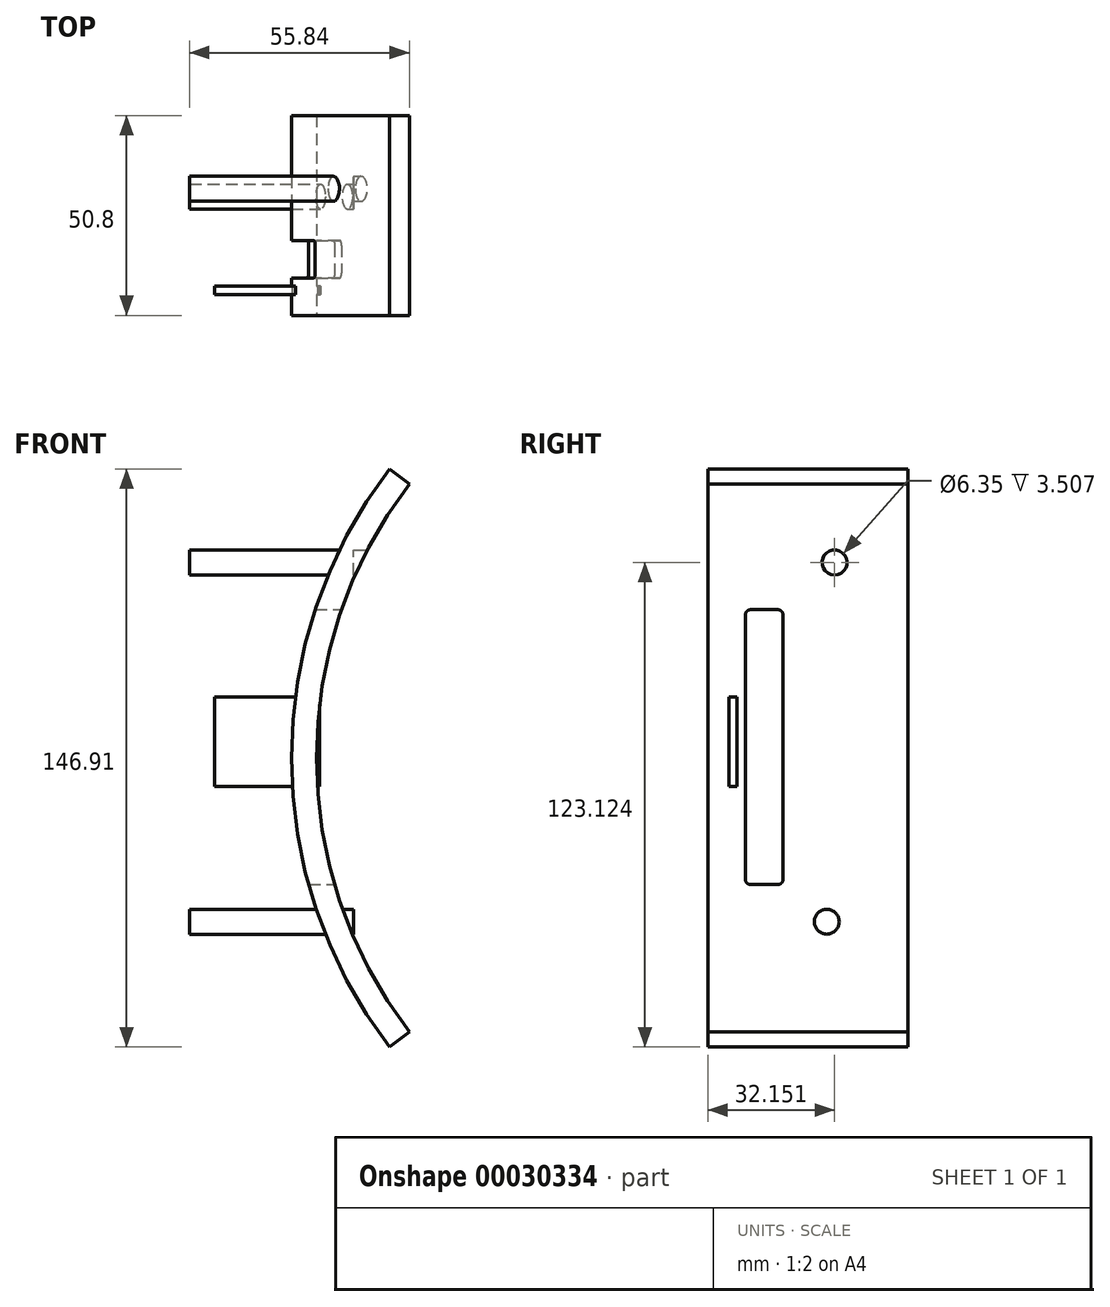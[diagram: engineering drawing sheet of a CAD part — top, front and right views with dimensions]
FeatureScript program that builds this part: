
annotation { "Feature Type Name" : "Feature", "Feature Type Description" : "" }
export const myFeature = defineFeature(function(context is Context, id is Id, definition is map)
    precondition{}
    {
        {
            var Q0;
            Q0=qCreatedBy(makeId("Front.planeOp"),FACE);
            var sketch = newSketch(context, id + "F0", { "sketchPlane" : qUnion([Q0])});
            skArc(sketch, "E0", {"start": v(0, 69.33) * mm, "mid": v(-24.94, -4.12) * mm, "end": v(0, -77.58) * mm});
            skArc(sketch, "E1.0", {"start": v(5.04, 65.47) * mm, "mid": v(-18.59, -4.12) * mm, "end": v(5.04, -73.71) * mm});
            skLineSegment(sketch, "E2", {"start": v(5.04, 65.47) * mm, "end": v(0, 69.33) * mm});
            skLineSegment(sketch, "E3", {"start": v(5.04, -73.71) * mm, "end": v(0, -77.58) * mm});
            skSolve(sketch);
        }
        {
            var Q0;
            Q0=makeQuery(id+"F0.imprint","IMPRINT",FACE,{"disambiguationData":[TD([[makeQuery(id+"F0.imprint","IMPRINT",EDGE,{"derivedFrom":sQuery(id+"F0.wireOp",EDGE,"E0")}),1.0]])]});
            extrude(context, id + "F1", {"entities" : qUnion([Q0]), "oppositeDirection" : true, "depth" : 50.8 * mm});
        }
        {
            var Q0;
            Q0=qCreatedBy(makeId("Right.planeOp"),FACE);
            var sketch = newSketch(context, id + "F2", { "sketchPlane" : qUnion([Q0])});
            skLineSegment(sketch, "E4.bottom", {"start": v(10.78, 33.55) * mm, "end": v(17.77, 33.55) * mm});
            skLineSegment(sketch, "E4.top", {"start": v(10.78, -36.3) * mm, "end": v(17.77, -36.3) * mm});
            skLineSegment(sketch, "E4.left", {"start": v(9.51, 32.28) * mm, "end": v(9.51, -35.03) * mm});
            skLineSegment(sketch, "E4.right", {"start": v(19.04, 32.28) * mm, "end": v(19.04, -35.03) * mm});
            skPoint(sketch, "E5.visualSharp", {"position": v(19.04, 33.55) * mm});
            skArc(sketch, "E5.filletArc", {"start": v(19.04, 32.28) * mm, "mid": v(18.67, 33.18) * mm, "end": v(17.77, 33.55) * mm});
            skPoint(sketch, "E6.visualSharp", {"position": v(9.51, 33.55) * mm});
            skArc(sketch, "E6.filletArc", {"start": v(9.55, 33.55) * mm, "mid": v(9.52, 33.54) * mm, "end": v(9.51, 33.52) * mm});
            skPoint(sketch, "E7.visualSharp", {"position": v(19.04, -36.3) * mm});
            skArc(sketch, "E7.filletArc", {"start": v(17.77, -36.3) * mm, "mid": v(18.67, -35.93) * mm, "end": v(19.04, -35.03) * mm});
            skArc(sketch, "E8.filletArc", {"start": v(10.78, 33.55) * mm, "mid": v(9.89, 33.18) * mm, "end": v(9.51, 32.28) * mm});
            skPoint(sketch, "E9.visualSharp", {"position": v(9.51, -36.3) * mm});
            skArc(sketch, "E9.filletArc", {"start": v(9.51, -35.03) * mm, "mid": v(9.89, -35.93) * mm, "end": v(10.78, -36.3) * mm});
            skSolve(sketch);
        }
        {
            var Q0;
            Q0 = qSketchRegion(id + "F2", true);
            extrude(context, id + "F3", {"entities" : qUnion([Q0]), "operationType" : NewBodyOperationType.REMOVE, "oppositeDirection" : true, "depth" : 50.8 * mm});
        }
        {
            var Q0;
            Q0=qCreatedBy(makeId("Right.planeOp"),FACE);
            var sketch = newSketch(context, id + "F4", { "sketchPlane" : qUnion([Q0])});
            skCircle(sketch, "E10", {"center": v(30.17, -45.72) * mm, "radius": 3.18 * mm});
            skCircle(sketch, "E11", {"center": v(32.15, 45.54) * mm, "radius": 3.18 * mm});
            skSolve(sketch);
        }
        {
            var Q0;
            Q0=makeQuery(id+"F4.imprint","IMPRINT",FACE,{"disambiguationData":[TD([[makeQuery(id+"F4.imprint","IMPRINT",EDGE,{"derivedFrom":sQuery(id+"F4.wireOp",EDGE,"E11")}),1.0]])]});
            var Q1;
            Q1=makeQuery(id+"F4.imprint","IMPRINT",FACE,{"disambiguationData":[TD([[makeQuery(id+"F4.imprint","IMPRINT",EDGE,{"derivedFrom":sQuery(id+"F4.wireOp",EDGE,"E10")}),1.0]])]});
            var Q2;
            Q2=sQuery(id+"F4.wireOp",EDGE,"E11");
            extrude(context, id + "F5", {"entities" : qUnion([Q0, Q1]), "operationType" : NewBodyOperationType.ADD, "surfaceEntities" : qUnion([Q2]), "oppositeDirection" : true, "depth" : 50.8 * mm});
        }
        {
            var Q0;
            Q0=makeQuery(id+"F5.opExtrude","CAP_FACE",FACE,{"disambiguationData":[OSD([sQuery(id+"F4.wireOp",EDGE,"E11")])],"isStart":true});
            var Q1;
            Q1=makeQuery(id+"F5.opExtrude","CAP_FACE",FACE,{"disambiguationData":[OSD([sQuery(id+"F4.wireOp",EDGE,"E10")])],"isStart":true});
            extrude(context, id + "F6", {"entities" : qUnion([Q0, Q1]), "operationType" : NewBodyOperationType.REMOVE, "oppositeDirection" : true, "depth" : 9.14 * mm});
        }
        {
            var Q0;
            Q0=qCreatedBy(makeId("Right.planeOp"),FACE);
            var sketch = newSketch(context, id + "F7", { "sketchPlane" : qUnion([Q0])});
            skLineSegment(sketch, "E12.bottom", {"start": v(7.38, 11.34) * mm, "end": v(5.3, 11.34) * mm});
            skLineSegment(sketch, "E12.top", {"start": v(7.38, -11.3) * mm, "end": v(5.3, -11.3) * mm});
            skLineSegment(sketch, "E12.left", {"start": v(7.38, 11.34) * mm, "end": v(7.38, -11.3) * mm});
            skLineSegment(sketch, "E12.right", {"start": v(5.3, 11.34) * mm, "end": v(5.3, -11.3) * mm});
            skSolve(sketch);
        }
        {
            var Q0;
            Q0=makeQuery(id+"F7.imprint","IMPRINT",FACE,{"disambiguationData":[TD([[makeQuery(id+"F7.imprint","IMPRINT",EDGE,{"derivedFrom":sQuery(id+"F7.wireOp",EDGE,"E12.bottom")}),1.0]])]});
            var Q1;
            Q1=sQuery(id+"F7.wireOp",EDGE,"E12.right");
            var Q2;
            Q2=sQuery(id+"F7.wireOp",EDGE,"E12.bottom");
            var Q3;
            Q3=sQuery(id+"F7.wireOp",EDGE,"E12.top");
            var Q4;
            Q4=sQuery(id+"F7.wireOp",EDGE,"E12.left");
            extrude(context, id + "F8", {"entities" : qUnion([Q0]), "operationType" : NewBodyOperationType.ADD, "surfaceEntities" : qUnion([Q1, Q2, Q3, Q4]), "oppositeDirection" : true, "depth" : 44.45 * mm});
        }
        {
            var Q0;
            Q0=makeQuery(id+"F8.opExtrude","CAP_FACE",FACE,{"disambiguationData":[OSD([sQuery(id+"F7.wireOp",EDGE,"E12.bottom"),sQuery(id+"F7.wireOp",EDGE,"E12.top"),sQuery(id+"F7.wireOp",EDGE,"E12.left"),sQuery(id+"F7.wireOp",EDGE,"E12.right")])],"isStart":true});
            extrude(context, id + "F9", {"entities" : qUnion([Q0]), "operationType" : NewBodyOperationType.REMOVE, "oppositeDirection" : true, "depth" : 17.78 * mm});
        }
    });
